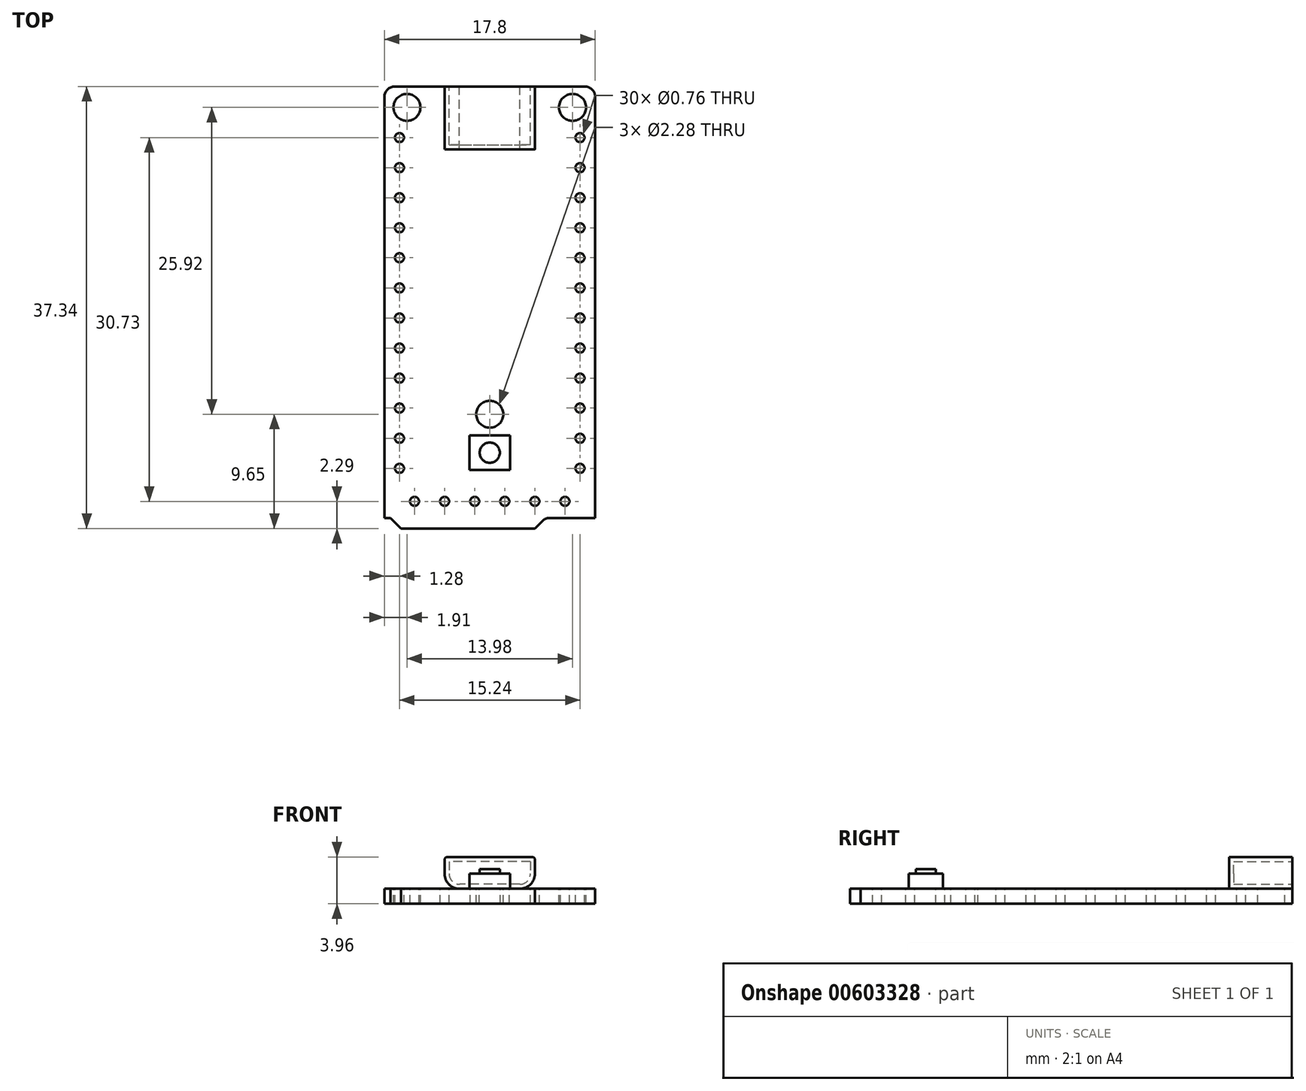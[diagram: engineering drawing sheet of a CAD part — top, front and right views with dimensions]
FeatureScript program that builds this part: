
annotation { "Feature Type Name" : "Feature", "Feature Type Description" : "" }
export const myFeature = defineFeature(function(context is Context, id is Id, definition is map)
    precondition{}
    {
        {
            var Q0;
            Q0=qCreatedBy(makeId("Top.planeOp"),FACE);
            var sketch = newSketch(context, id + "F0", { "sketchPlane" : qUnion([Q0])});
            skLineSegment(sketch, "E0.bottom", {"start": v(-8.89, 18.67) * mm, "end": v(8.9, 18.67) * mm});
            skLineSegment(sketch, "E0.top", {"start": v(-8.9, -18.67) * mm, "end": v(8.89, -18.67) * mm});
            skLineSegment(sketch, "E0.left", {"start": v(-8.89, 18.67) * mm, "end": v(-8.9, -18.67) * mm});
            skLineSegment(sketch, "E0.right", {"start": v(8.9, 18.67) * mm, "end": v(8.89, -18.67) * mm});
            skLineSegment(sketch, "E1", {"start": v(8.9, 18.67) * mm, "end": v(-8.89, -18.67) * mm, "construction": true});
            skSolve(sketch);
        }
        {
            var Q0;
            Q0 = qSketchRegion(id + "F0", true);
            extrude(context, id + "F1", {"entities" : qUnion([Q0]), "depth" : 1.27 * mm, "offsetDistance" : 25.4 * mm});
        }
        {
            var Q0;
            Q0=makeQuery(id+"F1.opExtrude","CAP_FACE",FACE,{"disambiguationData":[OSD([sQuery(id+"F0.wireOp",EDGE,"E0.bottom"),sQuery(id+"F0.wireOp",EDGE,"E0.top"),sQuery(id+"F0.wireOp",EDGE,"E0.left"),sQuery(id+"F0.wireOp",EDGE,"E0.right")])],"isStart":false});
            var sketch = newSketch(context, id + "F2", { "sketchPlane" : qUnion([Q0])});
            skCircle(sketch, "E2", {"center": v(6.99, 16.9) * mm, "radius": 1.14 * mm});
            skLineSegment(sketch, "E3", {"start": v(0, 0) * mm, "end": v(0, 35.9) * mm, "construction": true});
            skCircle(sketch, "E4.MirrorC", {"center": v(-6.99, 16.9) * mm, "radius": 1.14 * mm});
            skCircle(sketch, "E5", {"center": v(0, -9.02) * mm, "radius": 1.14 * mm});
            skSolve(sketch);
        }
        {
            var Q0;
            Q0 = qSketchRegion(id + "F2", true);
            extrude(context, id + "F3", {"entities" : qUnion([Q0]), "operationType" : NewBodyOperationType.REMOVE, "endBound" : BoundingType.UP_TO_NEXT, "oppositeDirection" : true, "depth" : 25.4 * mm, "offsetDistance" : 25.4 * mm});
        }
        {
            var Q0;
            Q0=makeQuery(id+"F1.opExtrude","CAP_FACE",FACE,{"disambiguationData":[OSD([sQuery(id+"F0.wireOp",EDGE,"E0.bottom"),sQuery(id+"F0.wireOp",EDGE,"E0.top"),sQuery(id+"F0.wireOp",EDGE,"E0.left"),sQuery(id+"F0.wireOp",EDGE,"E0.right")])],"isStart":false});
            var sketch = newSketch(context, id + "F4", { "sketchPlane" : qUnion([Q0])});
            skLineSegment(sketch, "E6.top", {"start": v(-8.9, -18.67) * mm, "end": v(-7.5, -18.67) * mm});
            skLineSegment(sketch, "E6.left", {"start": v(-8.9, -17.78) * mm, "end": v(-8.9, -18.67) * mm});
            skLineSegment(sketch, "E6.right", {"start": v(8.89, -17.78) * mm, "end": v(8.89, -18.67) * mm});
            skLineSegment(sketch, "E7", {"start": v(-8.38, -17.78) * mm, "end": v(-7.5, -18.67) * mm});
            skLineSegment(sketch, "E8", {"start": v(4.7, -17.78) * mm, "end": v(3.8, -18.67) * mm});
            skLineSegment(sketch, "E9.trimOffspring", {"start": v(4.7, -17.78) * mm, "end": v(8.89, -17.78) * mm});
            skLineSegment(sketch, "E10.trimOffspring", {"start": v(3.8, -18.67) * mm, "end": v(8.89, -18.67) * mm});
            skLineSegment(sketch, "E11", {"start": v(-8.9, -17.78) * mm, "end": v(-8.38, -17.78) * mm});
            skSolve(sketch);
        }
        {
            var Q0;
            Q0 = qSketchRegion(id + "F4", true);
            extrude(context, id + "F5", {"entities" : qUnion([Q0]), "operationType" : NewBodyOperationType.REMOVE, "oppositeDirection" : true, "depth" : 25.4 * mm, "offsetDistance" : 25.4 * mm});
        }
        {
            var Q0;
            Q0=makeQuery(id+"F1.opExtrude","SWEPT_EDGE",EDGE,{"disambiguationData":[OSD([sQuery(id+"F0.wireOp",EDGE,"E0.bottom"),sQuery(id+"F0.wireOp",EDGE,"E0.right")])]});
            var Q1;
            Q1=makeQuery(id+"F1.opExtrude","SWEPT_EDGE",EDGE,{"disambiguationData":[OSD([sQuery(id+"F0.wireOp",EDGE,"E0.bottom"),sQuery(id+"F0.wireOp",EDGE,"E0.left")])]});
            var Q2;
            Q2=makeQuery(id+"F1.opExtrude","SWEPT_EDGE",EDGE,{"disambiguationData":[OSD([sQuery(id+"F0.wireOp",EDGE,"E0.top"),sQuery(id+"F0.wireOp",EDGE,"E0.right")])]});
            var Q3;
            Q3=makeQuery(id+"F1.opExtrude","SWEPT_EDGE",EDGE,{"disambiguationData":[OSD([sQuery(id+"F0.wireOp",EDGE,"E0.top"),sQuery(id+"F0.wireOp",EDGE,"E0.left")])]});
            var Q4;
            Q4=makeQuery(id+"F5.boolean.opBoolean","COPY",EDGE,{"derivedFrom":makeQuery(id+"F5.opExtrude","SWEPT_EDGE",EDGE,{"disambiguationData":[OSD([sQuery(id+"F4.wireOp",EDGE,"E8"),sQuery(id+"F4.wireOp",EDGE,"E9.trimOffspring")])]})});
            var Q5;
            Q5=makeQuery(id+"F5.boolean.opBoolean","COPY",EDGE,{"derivedFrom":makeQuery(id+"F5.opExtrude","SWEPT_EDGE",EDGE,{"disambiguationData":[OSD([sQuery(id+"F0.wireOp",EDGE,"E0.right"),sQuery(id+"F4.wireOp",EDGE,"E6.right"),sQuery(id+"F4.wireOp",EDGE,"E9.trimOffspring")])]})});
            var Q6;
            Q6=makeQuery(id+"F5.boolean.opBoolean","COPY",EDGE,{"derivedFrom":makeQuery(id+"F5.opExtrude","SWEPT_EDGE",EDGE,{"disambiguationData":[OSD([sQuery(id+"F0.wireOp",EDGE,"E0.left"),sQuery(id+"F4.wireOp",EDGE,"E6.left"),sQuery(id+"F4.wireOp",EDGE,"E11")])]})});
            fillet(context, id + "F6", {"entities" : qUnion([Q0, Q1, Q2, Q3, Q4, Q5, Q6]), "radius" : 0.89 * mm, "tangentPropagation" : true, "allowEdgeOverflow" : false});
        }
        {
            var Q0;
            Q0=makeQuery(id+"F1.opExtrude","SWEPT_FACE",FACE,{"disambiguationData":[OSD([sQuery(id+"F0.wireOp",EDGE,"E0.bottom")])]});
            var sketch = newSketch(context, id + "F7", { "sketchPlane" : qUnion([Q0])});
            skLineSegment(sketch, "E12", {"start": v(0, -2.2) * mm, "end": v(0, 0) * mm, "construction": true});
            skLineSegment(sketch, "E13.bottom", {"start": v(0, 3.96) * mm, "end": v(3.81, 3.96) * mm});
            skLineSegment(sketch, "E13.top", {"start": v(0, 1.27) * mm, "end": v(2.54, 1.27) * mm});
            skLineSegment(sketch, "E13.right", {"start": v(3.81, 3.96) * mm, "end": v(3.81, 2.54) * mm});
            skPoint(sketch, "E14.visualSharp", {"position": v(3.81, 1.27) * mm});
            skArc(sketch, "E14.filletArc", {"start": v(2.54, 1.27) * mm, "mid": v(3.44, 1.64) * mm, "end": v(3.81, 2.54) * mm});
            skLineSegment(sketch, "E15.MirrorCS", {"start": v(0, 3.96) * mm, "end": v(-3.81, 3.96) * mm});
            skLineSegment(sketch, "E16.MirrorCS", {"start": v(-3.81, 3.96) * mm, "end": v(-3.81, 2.54) * mm});
            skArc(sketch, "E17.MirrorCS", {"start": v(-2.54, 1.27) * mm, "mid": v(-3.44, 1.64) * mm, "end": v(-3.81, 2.54) * mm});
            skLineSegment(sketch, "E18.MirrorCS", {"start": v(0, 1.27) * mm, "end": v(-2.54, 1.27) * mm});
            skSolve(sketch);
        }
        {
            var Q0;
            Q0=makeQuery(id+"F7.imprint","IMPRINT",FACE,{"disambiguationData":[TD([[makeQuery(id+"F7.imprint","IMPRINT",EDGE,{"derivedFrom":sQuery(id+"F7.wireOp",EDGE,"E13.bottom")}),-1.0]])]});
            extrude(context, id + "F8", {"entities" : qUnion([Q0]), "operationType" : NewBodyOperationType.ADD, "oppositeDirection" : true, "depth" : 5.33 * mm, "offsetDistance" : 25.4 * mm});
        }
        {
            var Q0;
            Q0=makeQuery(id+"F1.opExtrude","CAP_FACE",FACE,{"disambiguationData":[OSD([sQuery(id+"F0.wireOp",EDGE,"E0.bottom"),sQuery(id+"F0.wireOp",EDGE,"E0.top"),sQuery(id+"F0.wireOp",EDGE,"E0.left"),sQuery(id+"F0.wireOp",EDGE,"E0.right")])],"isStart":false});
            var sketch = newSketch(context, id + "F9", { "sketchPlane" : qUnion([Q0])});
            skCircle(sketch, "E19", {"center": v(7.62, 14.35) * mm, "radius": 0.38 * mm});
            skLineSegment(sketch, "E20", {"start": v(0, 0) * mm, "end": v(0, 9.72) * mm, "construction": true});
            skCircle(sketch, "E21.1.0.0", {"center": v(7.62, 11.81) * mm, "radius": 0.38 * mm});
            skCircle(sketch, "E21.2.0.0", {"center": v(7.62, 9.27) * mm, "radius": 0.38 * mm});
            skCircle(sketch, "E21.3.0.0", {"center": v(7.62, 6.73) * mm, "radius": 0.38 * mm});
            skCircle(sketch, "E21.4.0.0", {"center": v(7.62, 4.2) * mm, "radius": 0.38 * mm});
            skCircle(sketch, "E21.5.0.0", {"center": v(7.62, 1.65) * mm, "radius": 0.38 * mm});
            skCircle(sketch, "E21.6.0.0", {"center": v(7.62, -0.89) * mm, "radius": 0.38 * mm});
            skCircle(sketch, "E21.7.0.0", {"center": v(7.62, -3.43) * mm, "radius": 0.38 * mm});
            skCircle(sketch, "E21.8.0.0", {"center": v(7.62, -5.97) * mm, "radius": 0.38 * mm});
            skCircle(sketch, "E21.9.0.0", {"center": v(7.62, -8.5) * mm, "radius": 0.38 * mm});
            skCircle(sketch, "E21.10.0.0", {"center": v(7.62, -11.05) * mm, "radius": 0.38 * mm});
            skCircle(sketch, "E21.11.0.0", {"center": v(7.62, -13.59) * mm, "radius": 0.38 * mm});
            skLineSegment(sketch, "E21.direction1", {"start": v(7.62, 14.35) * mm, "end": v(7.62, 11.81) * mm, "construction": true});
            skCircle(sketch, "E22.MirrorC", {"center": v(-7.62, -13.59) * mm, "radius": 0.38 * mm});
            skCircle(sketch, "E23.MirrorC", {"center": v(-7.62, -11.05) * mm, "radius": 0.38 * mm});
            skCircle(sketch, "E24.MirrorC", {"center": v(-7.62, -8.5) * mm, "radius": 0.38 * mm});
            skCircle(sketch, "E25.MirrorC", {"center": v(-7.62, -5.97) * mm, "radius": 0.38 * mm});
            skCircle(sketch, "E26.MirrorC", {"center": v(-7.62, -3.43) * mm, "radius": 0.38 * mm});
            skCircle(sketch, "E27.MirrorC", {"center": v(-7.62, -0.89) * mm, "radius": 0.38 * mm});
            skCircle(sketch, "E28.MirrorC", {"center": v(-7.62, 1.65) * mm, "radius": 0.38 * mm});
            skCircle(sketch, "E29.MirrorC", {"center": v(-7.62, 4.2) * mm, "radius": 0.38 * mm});
            skCircle(sketch, "E30.MirrorC", {"center": v(-7.62, 6.73) * mm, "radius": 0.38 * mm});
            skCircle(sketch, "E31.MirrorC", {"center": v(-7.62, 9.27) * mm, "radius": 0.38 * mm});
            skCircle(sketch, "E32.MirrorC", {"center": v(-7.62, 11.81) * mm, "radius": 0.38 * mm});
            skCircle(sketch, "E33.MirrorC", {"center": v(-7.62, 14.35) * mm, "radius": 0.38 * mm});
            skSolve(sketch);
        }
        {
            var Q0;
            Q0 = qSketchRegion(id + "F9", true);
            extrude(context, id + "F10", {"entities" : qUnion([Q0]), "operationType" : NewBodyOperationType.REMOVE, "endBound" : BoundingType.UP_TO_NEXT, "oppositeDirection" : true, "depth" : 25.4 * mm, "offsetDistance" : 25.4 * mm});
        }
        {
            var Q0;
            Q0=makeQuery(id+"F1.opExtrude","CAP_FACE",FACE,{"disambiguationData":[OSD([sQuery(id+"F0.wireOp",EDGE,"E0.bottom"),sQuery(id+"F0.wireOp",EDGE,"E0.top"),sQuery(id+"F0.wireOp",EDGE,"E0.left"),sQuery(id+"F0.wireOp",EDGE,"E0.right")])],"isStart":false});
            var sketch = newSketch(context, id + "F11", { "sketchPlane" : qUnion([Q0])});
            skCircle(sketch, "E34", {"center": v(-6.35, -16.38) * mm, "radius": 0.38 * mm});
            skLineSegment(sketch, "E35", {"start": v(0, -17.65) * mm, "end": v(0, 0) * mm, "construction": true});
            skCircle(sketch, "E36.1.0.0", {"center": v(-3.81, -16.38) * mm, "radius": 0.38 * mm});
            skCircle(sketch, "E36.2.0.0", {"center": v(-1.27, -16.38) * mm, "radius": 0.38 * mm});
            skCircle(sketch, "E36.3.0.0", {"center": v(1.27, -16.38) * mm, "radius": 0.38 * mm});
            skCircle(sketch, "E36.4.0.0", {"center": v(3.81, -16.38) * mm, "radius": 0.38 * mm});
            skCircle(sketch, "E36.5.0.0", {"center": v(6.35, -16.38) * mm, "radius": 0.38 * mm});
            skLineSegment(sketch, "E36.direction1", {"start": v(-6.35, -16.38) * mm, "end": v(-3.81, -16.38) * mm, "construction": true});
            skSolve(sketch);
        }
        {
            var Q0;
            Q0 = qSketchRegion(id + "F11", true);
            extrude(context, id + "F12", {"entities" : qUnion([Q0]), "operationType" : NewBodyOperationType.REMOVE, "endBound" : BoundingType.UP_TO_NEXT, "oppositeDirection" : true, "depth" : 25.4 * mm, "offsetDistance" : 25.4 * mm});
        }
        {
            var Q0;
            Q0=makeQuery(id+"F8.boolean.opBoolean","MERGE",FACE,{"derivedFrom":[makeQuery(id+"F1.opExtrude","SWEPT_FACE",FACE,{"disambiguationData":[OSD([sQuery(id+"F0.wireOp",EDGE,"E0.bottom")])]}),makeQuery(id+"F8.opExtrude","CAP_FACE",FACE,{"disambiguationData":[OSD([sQuery(id+"F7.wireOp",EDGE,"E13.bottom"),sQuery(id+"F7.wireOp",EDGE,"E13.top"),sQuery(id+"F7.wireOp",EDGE,"E13.right"),sQuery(id+"F7.wireOp",EDGE,"E14.filletArc"),sQuery(id+"F7.wireOp",EDGE,"E15.MirrorCS"),sQuery(id+"F7.wireOp",EDGE,"E16.MirrorCS"),sQuery(id+"F7.wireOp",EDGE,"E17.MirrorCS"),sQuery(id+"F7.wireOp",EDGE,"E18.MirrorCS")])],"isStart":true})]});
            var sketch = newSketch(context, id + "F13", { "sketchPlane" : qUnion([Q0])});
            skArc(sketch, "E37.0", {"start": v(2.54, 1.65) * mm, "mid": v(3.17, 1.91) * mm, "end": v(3.43, 2.54) * mm});
            skArc(sketch, "E37.1", {"start": v(-2.54, 1.65) * mm, "mid": v(-3.17, 1.91) * mm, "end": v(-3.43, 2.54) * mm});
            skLineSegment(sketch, "E37.2", {"start": v(-3.43, 3.58) * mm, "end": v(-3.43, 2.54) * mm});
            skLineSegment(sketch, "E37.3", {"start": v(-3.43, 3.58) * mm, "end": v(3.43, 3.58) * mm});
            skLineSegment(sketch, "E37.4", {"start": v(3.43, 3.58) * mm, "end": v(3.43, 2.54) * mm});
            skLineSegment(sketch, "E38", {"start": v(-2.54, 1.65) * mm, "end": v(2.54, 1.65) * mm});
            skSolve(sketch);
        }
        {
            var Q0;
            Q0 = qSketchRegion(id + "F13", true);
            var Q1;
            Q1=makeQuery(id+"F8.opExtrude","CAP_FACE",FACE,{"disambiguationData":[OSD([sQuery(id+"F7.wireOp",EDGE,"E13.bottom"),sQuery(id+"F7.wireOp",EDGE,"E13.top"),sQuery(id+"F7.wireOp",EDGE,"E13.right"),sQuery(id+"F7.wireOp",EDGE,"E14.filletArc"),sQuery(id+"F7.wireOp",EDGE,"E15.MirrorCS"),sQuery(id+"F7.wireOp",EDGE,"E16.MirrorCS"),sQuery(id+"F7.wireOp",EDGE,"E17.MirrorCS"),sQuery(id+"F7.wireOp",EDGE,"E18.MirrorCS")])],"isStart":false});
            extrude(context, id + "F14", {"entities" : qUnion([Q0]), "operationType" : NewBodyOperationType.REMOVE, "endBound" : BoundingType.UP_TO_SURFACE, "oppositeDirection" : true, "depth" : 25.4 * mm, "endBoundEntityFace" : qUnion([Q1]), "hasOffset" : true, "offsetDistance" : 0.38 * mm});
        }
        {
            var Q0;
            Q0=makeQuery(id+"F8.opExtrude","SWEPT_EDGE",EDGE,{"disambiguationData":[OSD([sQuery(id+"F7.wireOp",EDGE,"E15.MirrorCS"),sQuery(id+"F7.wireOp",EDGE,"E16.MirrorCS")])]});
            var Q1;
            Q1=makeQuery(id+"F8.opExtrude","SWEPT_EDGE",EDGE,{"disambiguationData":[OSD([sQuery(id+"F7.wireOp",EDGE,"E13.bottom"),sQuery(id+"F7.wireOp",EDGE,"E13.right")])]});
            fillet(context, id + "F15", {"entities" : qUnion([Q0, Q1]), "radius" : 0.25 * mm, "tangentPropagation" : true, "allowEdgeOverflow" : false});
        }
        {
            var Q0;
            Q0=makeQuery(id+"F1.opExtrude","CAP_FACE",FACE,{"disambiguationData":[OSD([sQuery(id+"F0.wireOp",EDGE,"E0.bottom"),sQuery(id+"F0.wireOp",EDGE,"E0.top"),sQuery(id+"F0.wireOp",EDGE,"E0.left"),sQuery(id+"F0.wireOp",EDGE,"E0.right")])],"isStart":false});
            var sketch = newSketch(context, id + "F16", { "sketchPlane" : qUnion([Q0])});
            skLineSegment(sketch, "E39.bottom", {"start": v(-1.71, -13.72) * mm, "end": v(1.71, -13.72) * mm});
            skLineSegment(sketch, "E39.top", {"start": v(-1.71, -10.82) * mm, "end": v(1.71, -10.82) * mm});
            skLineSegment(sketch, "E39.left", {"start": v(-1.71, -10.82) * mm, "end": v(-1.71, -13.72) * mm});
            skLineSegment(sketch, "E39.right", {"start": v(1.71, -10.82) * mm, "end": v(1.71, -13.72) * mm});
            skLineSegment(sketch, "E40", {"start": v(0, 3.71) * mm, "end": v(0, -13.72) * mm, "construction": true});
            skSolve(sketch);
        }
        {
            var Q0;
            Q0 = qSketchRegion(id + "F16", true);
            extrude(context, id + "F17", {"entities" : qUnion([Q0]), "operationType" : NewBodyOperationType.ADD, "depth" : 1.27 * mm, "offsetDistance" : 25.4 * mm});
        }
        {
            var Q0;
            Q0=makeQuery(id+"F17.opExtrude","CAP_FACE",FACE,{"disambiguationData":[OSD([sQuery(id+"F16.wireOp",EDGE,"E39.bottom"),sQuery(id+"F16.wireOp",EDGE,"E39.top"),sQuery(id+"F16.wireOp",EDGE,"E39.left"),sQuery(id+"F16.wireOp",EDGE,"E39.right")])],"isStart":false});
            var sketch = newSketch(context, id + "F18", { "sketchPlane" : qUnion([Q0])});
            skCircle(sketch, "E41", {"center": v(0, -12.27) * mm, "radius": 0.85 * mm});
            skPoint(sketch, "E41.centerSnap0", {"position": v(0, -13.72) * mm});
            skPoint(sketch, "E41.centerSnap1", {"position": v(-1.71, -12.27) * mm});
            skSolve(sketch);
        }
        {
            var Q0;
            Q0 = qSketchRegion(id + "F18", true);
            extrude(context, id + "F19", {"entities" : qUnion([Q0]), "operationType" : NewBodyOperationType.ADD, "depth" : 0.4 * mm, "offsetDistance" : 25.4 * mm});
        }
    });
